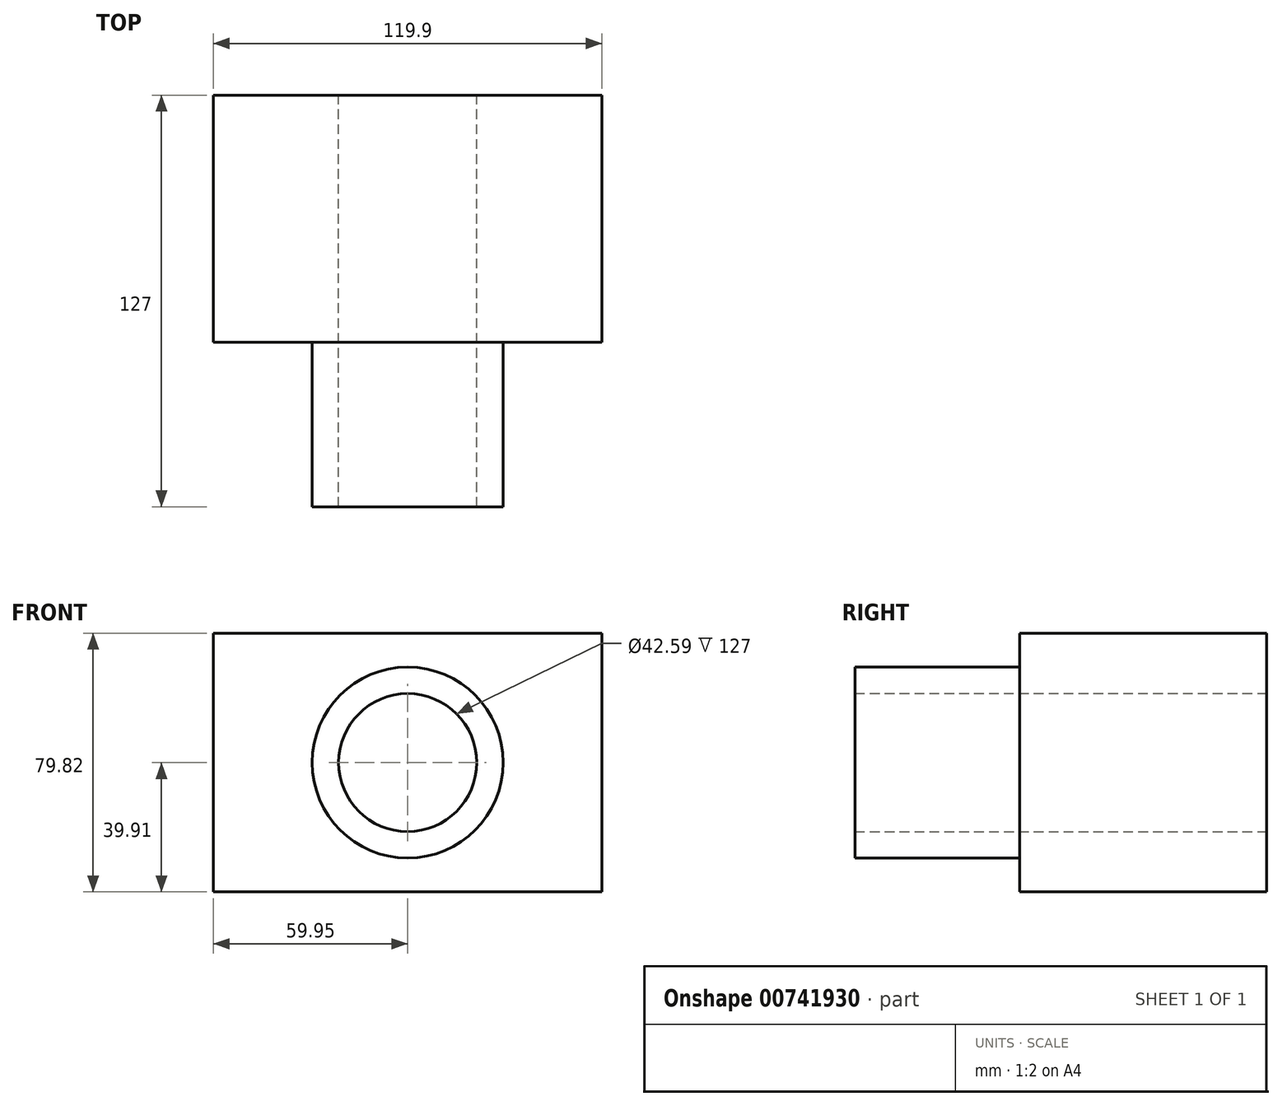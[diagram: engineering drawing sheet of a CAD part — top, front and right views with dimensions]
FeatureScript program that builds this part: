
annotation { "Feature Type Name" : "Feature", "Feature Type Description" : "" }
export const myFeature = defineFeature(function(context is Context, id is Id, definition is map)
    precondition{}
    {
        {
            var Q0;
            Q0=qCreatedBy(makeId("Front.planeOp"),FACE);
            var sketch = newSketch(context, id + "F0", { "sketchPlane" : qUnion([Q0])});
            skLineSegment(sketch, "E0.bottom", {"start": v(59.95, 39.9) * mm, "end": v(-59.95, 39.9) * mm});
            skLineSegment(sketch, "E0.top", {"start": v(59.95, -39.9) * mm, "end": v(-59.95, -39.9) * mm});
            skLineSegment(sketch, "E0.left", {"start": v(59.95, 39.9) * mm, "end": v(59.95, -39.9) * mm});
            skLineSegment(sketch, "E0.right", {"start": v(-59.95, 39.9) * mm, "end": v(-59.95, -39.9) * mm});
            skPoint(sketch, "E0.middle", {"position": v(0, 0) * mm});
            skCircle(sketch, "E1", {"center": v(0, 0) * mm, "radius": 22.15 * mm});
            skSolve(sketch);
        }
        {
            var Q0;
            Q0=qCreatedBy(makeId("Front.planeOp"),FACE);
            var sketch = newSketch(context, id + "F1", { "sketchPlane" : qUnion([Q0])});
            skCircle(sketch, "E2", {"center": v(0, 0) * mm, "radius": 29.46 * mm});
            skCircle(sketch, "E3", {"center": v(0, 0) * mm, "radius": 21.3 * mm});
            skSolve(sketch);
        }
        {
            var Q0;
            Q0 = qSketchRegion(id + "F0", true);
            extrude(context, id + "F2", {"entities" : qUnion([Q0]), "depth" : 76.2 * mm, "offsetDistance" : 25.4 * mm});
        }
        {
            var Q0;
            Q0 = qSketchRegion(id + "F1", true);
            extrude(context, id + "F3", {"entities" : qUnion([Q0]), "operationType" : NewBodyOperationType.ADD, "depth" : 127 * mm, "offsetDistance" : 25.4 * mm});
        }
    });
